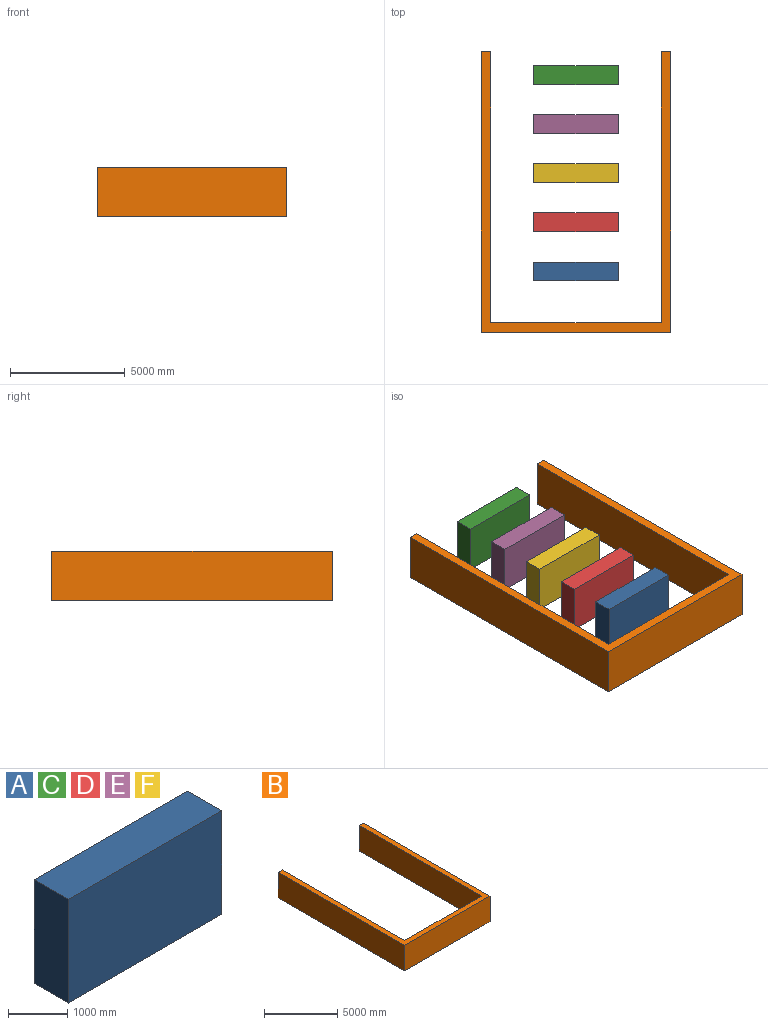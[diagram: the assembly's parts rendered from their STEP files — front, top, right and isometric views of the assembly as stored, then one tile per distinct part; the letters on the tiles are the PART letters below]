
ASSEMBLY  parts=6 mates=1
PART A: 6 faces, bbox 3657.6x812.8x2133.6 mm
  f0: plane 3657.6x2133.6mm, normal (0,-1,0), area 7803855.4mm2, adj f1,f3,f4,f5
  f1: plane 2133.6x812.8mm, normal (1,0,0), area 1734190.1mm2, adj f0,f2,f4,f5
  f2: plane 3657.6x2133.6mm, normal (0,1,0), area 7803855.4mm2, adj f1,f3,f4,f5
  f3: plane 2133.6x812.8mm, normal (-1,0,0), area 1734190.1mm2, adj f0,f2,f4,f5
  f4: plane 3657.6x812.8mm, normal (0,0,1), area 2972897.3mm2, adj f0,f1,f2,f3
  f5: plane 3657.6x812.8mm, normal (0,0,-1), area 2972897.3mm2, adj f0,f1,f2,f3
PART B: 10 faces, bbox 8229.6x12192x2133.6 mm
  f0: plane 11785.6x2133.6mm, normal (-1,0,0), area 25145756.2mm2, adj f3,f4,f5,f9
  f1: plane 8229.6x2133.6mm, normal (0,-1,0), area 17558674.6mm2, adj f2,f4,f5,f6
  f2: plane 12192x2133.6mm, normal (1,0,0), area 26012851.2mm2, adj f1,f3,f4,f5
  f3: plane 2133.6x406.4mm, normal (0,1,0), area 867095mm2, adj f0,f2,f4,f5
  f4: plane 12192x8229.6mm, normal (0,0,1), area 12923845.1mm2, adj f0,f1,f2,f3,f6,f7,f8,f9
  f5: plane 12192x8229.6mm, normal (0,0,-1), area 12923845.1mm2, adj f0,f1,f2,f3,f6,f7,f8,f9
  f6: plane 12192x2133.6mm, normal (-1,0,0), area 26012851.2mm2, adj f1,f4,f5,f8
  f7: plane 11785.6x2133.6mm, normal (1,0,0), area 25145756.2mm2, adj f4,f5,f8,f9
  f8: plane 2133.6x406.4mm, normal (0,1,0), area 867095mm2, adj f4,f5,f6,f7
  f9: plane 7416.8x2133.6mm, normal (0,1,0), area 15824484.5mm2, adj f0,f4,f5,f7
PART C: same geometry as A
PART D: same geometry as A
PART E: same geometry as A
PART F: same geometry as A
PLACE A t=(5.08,-50.8,0)mm
PLACE B at identity fixed
PLACE C t=(5.08,8483.6,0)mm
PLACE D t=(5.08,2082.8,0)mm
PLACE E t=(5.08,6350,0)mm
PLACE F t=(5.08,4216.4,0)mm
MATE fastened A.f5 <-> B.f5  axis (0,0,-1) through (0,-5994.4,0)mm
